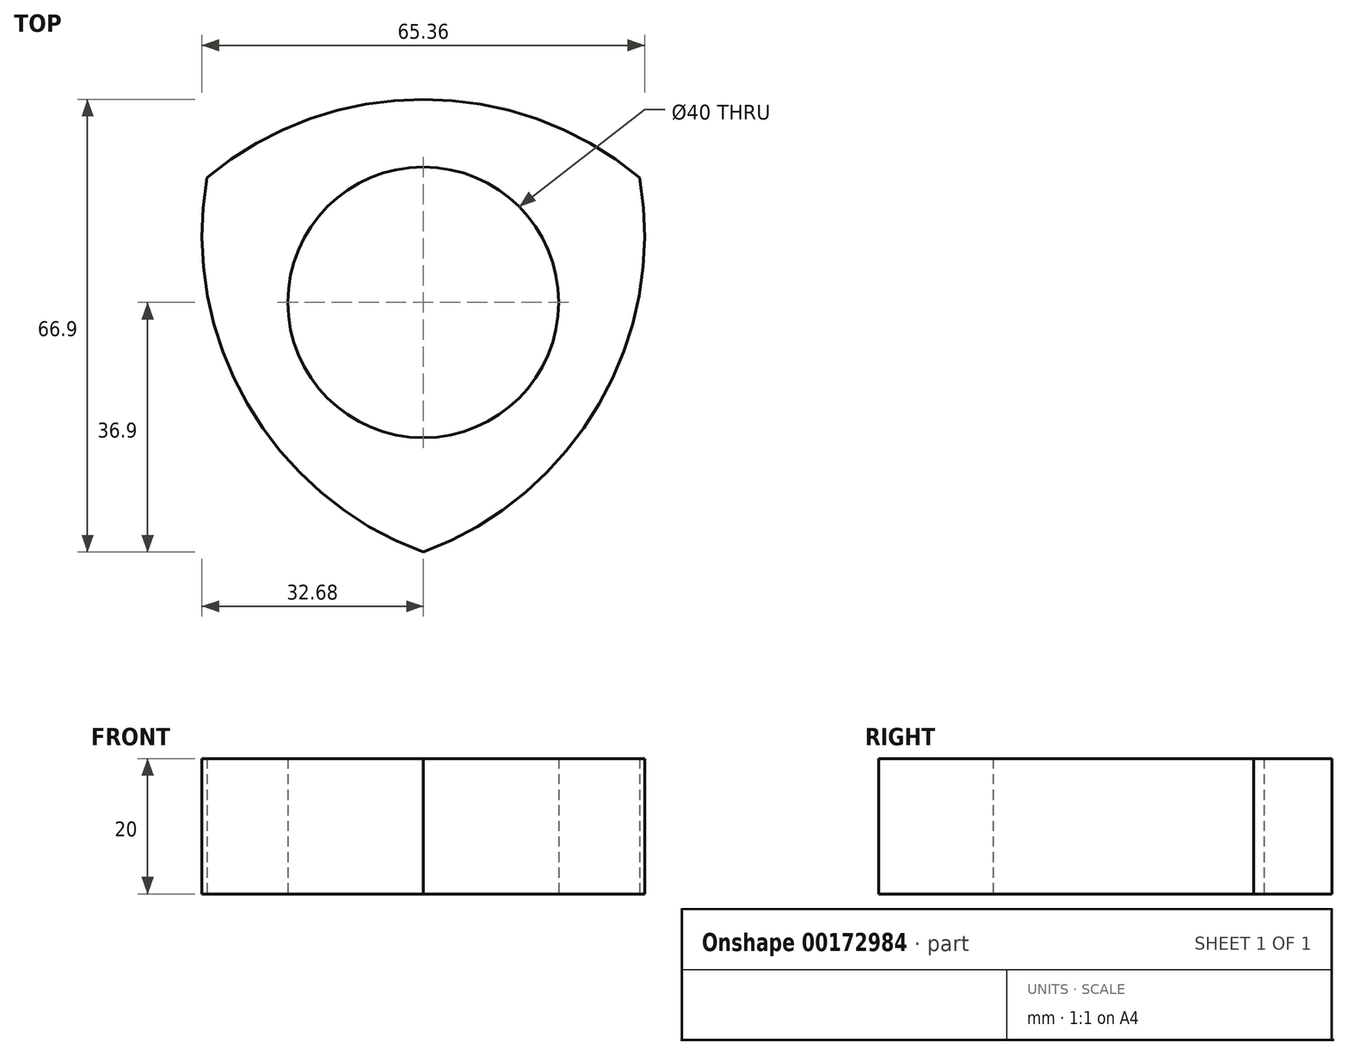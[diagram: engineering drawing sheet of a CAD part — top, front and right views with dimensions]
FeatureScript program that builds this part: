
annotation { "Feature Type Name" : "Feature", "Feature Type Description" : "" }
export const myFeature = defineFeature(function(context is Context, id is Id, definition is map)
    precondition{}
    {
        {
            var Q0;
            Q0=qCreatedBy(makeId("Top.planeOp"),FACE);
            var sketch = newSketch(context, id + "F0", { "sketchPlane" : qUnion([Q0])});
            skArc(sketch, "E0", {"start": v(-31.96, 18.45) * mm, "mid": v(0, 30) * mm, "end": v(31.96, 18.45) * mm});
            skArc(sketch, "E1.1.0", {"start": v(0, -36.9) * mm, "mid": v(-25.98, -15) * mm, "end": v(-31.96, 18.45) * mm});
            skArc(sketch, "E1.2.0", {"start": v(31.96, 18.45) * mm, "mid": v(25.98, -15) * mm, "end": v(0, -36.9) * mm});
            skPoint(sketch, "E1.center", {"position": v(0, 0) * mm});
            skSolve(sketch);
        }
        {
            var Q0;
            Q0 = qSketchRegion(id + "F0", true);
            extrude(context, id + "F1", {"entities" : qUnion([Q0]), "depth" : 20 * mm});
        }
        {
            var Q0;
            Q0=makeQuery(id+"F1.opExtrude","CAP_FACE",FACE,{"disambiguationData":[OSD([sQuery(id+"F0.wireOp",EDGE,"E0"),sQuery(id+"F0.wireOp",EDGE,"E1.1.0"),sQuery(id+"F0.wireOp",EDGE,"E1.2.0")])],"isStart":true});
            var sketch = newSketch(context, id + "F2", { "sketchPlane" : qUnion([Q0])});
            skCircle(sketch, "E2", {"center": v(0, 0) * mm, "radius": 20 * mm});
            skSolve(sketch);
        }
        {
            var Q0;
            Q0 = qSketchRegion(id + "F2", true);
            extrude(context, id + "F3", {"entities" : qUnion([Q0]), "operationType" : NewBodyOperationType.REMOVE, "oppositeDirection" : true, "depth" : 20 * mm});
        }
    });
